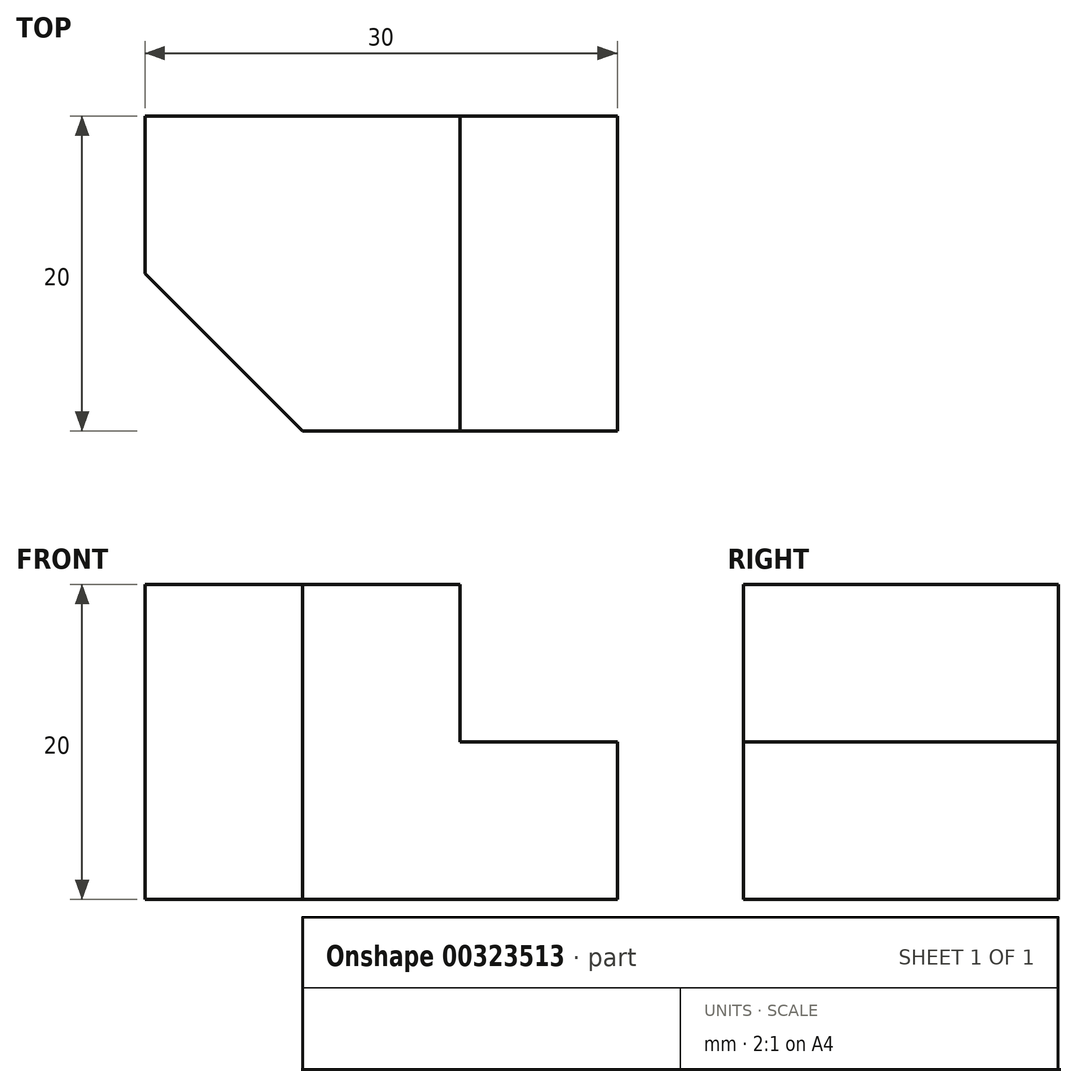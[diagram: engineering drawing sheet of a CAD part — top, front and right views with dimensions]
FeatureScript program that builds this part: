
annotation { "Feature Type Name" : "Feature", "Feature Type Description" : "" }
export const myFeature = defineFeature(function(context is Context, id is Id, definition is map)
    precondition{}
    {
        {
            var Q0;
            Q0=qCreatedBy(makeId("Top.planeOp"),FACE);
            var sketch = newSketch(context, id + "F0", { "sketchPlane" : qUnion([Q0])});
            skLineSegment(sketch, "E0", {"start": v(-31.04, 31.53) * mm, "end": v(-1.04, 31.53) * mm});
            skLineSegment(sketch, "E1", {"start": v(-1.04, 31.53) * mm, "end": v(-1.04, 11.53) * mm});
            skLineSegment(sketch, "E2", {"start": v(-1.04, 11.53) * mm, "end": v(-21.04, 11.53) * mm});
            skLineSegment(sketch, "E3", {"start": v(-31.04, 31.53) * mm, "end": v(-31.04, 21.53) * mm});
            skLineSegment(sketch, "E4", {"start": v(-31.04, 21.53) * mm, "end": v(-21.04, 11.53) * mm});
            skSolve(sketch);
        }
        {
            var Q0;
            Q0 = qSketchRegion(id + "F0", true);
            extrude(context, id + "F1", {"entities" : qUnion([Q0]), "oppositeDirection" : true, "depth" : 20 * mm});
        }
        {
            var Q0;
            Q0=makeQuery(id+"F1.opExtrude","SWEPT_FACE",FACE,{"disambiguationData":[OSD([sQuery(id+"F0.wireOp",EDGE,"E2")])]});
            var sketch = newSketch(context, id + "F2", { "sketchPlane" : qUnion([Q0])});
            skLineSegment(sketch, "E5", {"start": v(-1.04, -10) * mm, "end": v(-11.04, -10) * mm});
            skPoint(sketch, "E5.endSnap0", {"position": v(-1.04, -10) * mm});
            skLineSegment(sketch, "E6", {"start": v(-11.04, -10) * mm, "end": v(-11.04, 0) * mm});
            skLineSegment(sketch, "E7", {"start": v(-11.04, 0) * mm, "end": v(-1.04, 0) * mm});
            skLineSegment(sketch, "E8", {"start": v(-1.04, 0) * mm, "end": v(-1.04, -10) * mm});
            skSolve(sketch);
        }
        {
            var Q0;
            Q0 = qSketchRegion(id + "F2", true);
            extrude(context, id + "F3", {"entities" : qUnion([Q0]), "operationType" : NewBodyOperationType.REMOVE, "oppositeDirection" : true, "depth" : 25 * mm});
        }
    });
